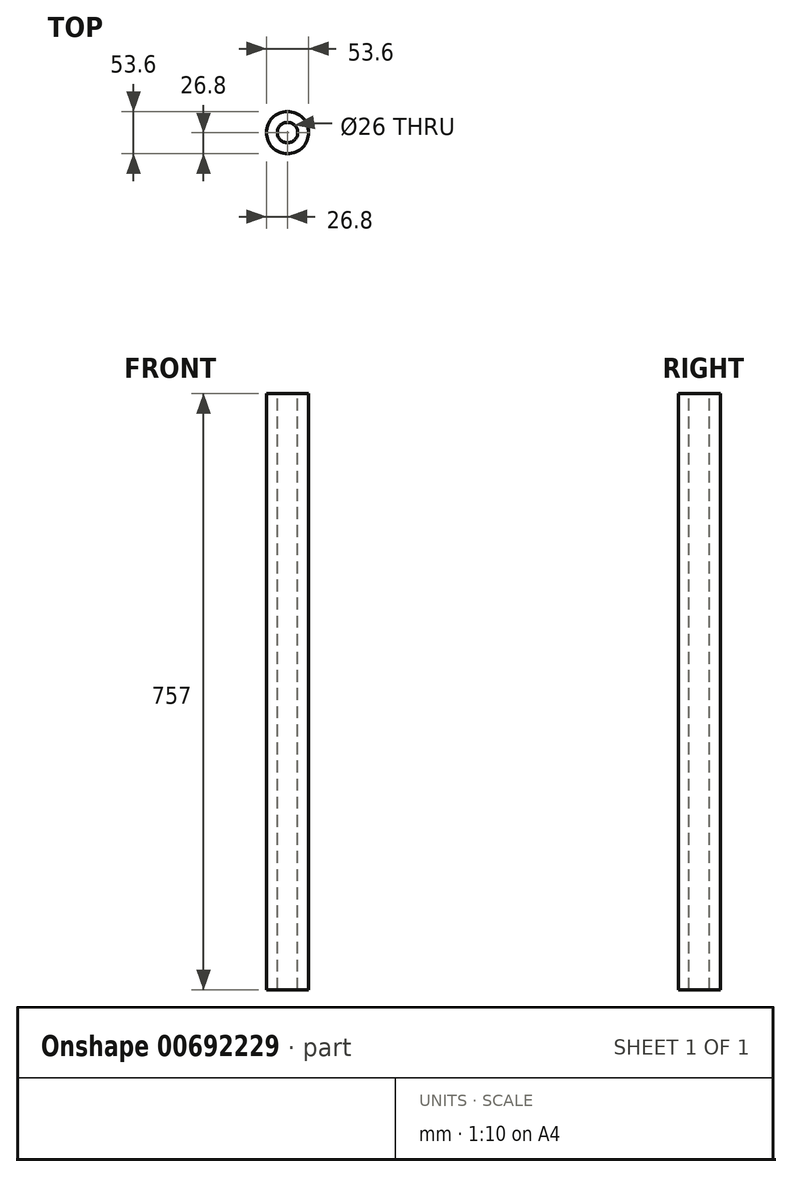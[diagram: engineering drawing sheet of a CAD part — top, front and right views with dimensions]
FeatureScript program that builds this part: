
annotation { "Feature Type Name" : "Feature", "Feature Type Description" : "" }
export const myFeature = defineFeature(function(context is Context, id is Id, definition is map)
    precondition{}
    {
        {
            var Q0;
            Q0=qCreatedBy(makeId("Front.planeOp"),FACE);
            var sketch = newSketch(context, id + "F0", { "sketchPlane" : qUnion([Q0])});
            skLineSegment(sketch, "E0", {"start": v(-26.8, 0) * mm, "end": v(-26.8, 757) * mm});
            skLineSegment(sketch, "E1", {"start": v(-26.8, 757) * mm, "end": v(-13, 757) * mm});
            skLineSegment(sketch, "E2", {"start": v(-13, 757) * mm, "end": v(-13, 0) * mm});
            skLineSegment(sketch, "E3", {"start": v(-13, 0) * mm, "end": v(-26.8, 0) * mm});
            skSolve(sketch);
        }
        {
            var Q0;
            Q0=qCreatedBy(makeId("Front.planeOp"),FACE);
            var sketch = newSketch(context, id + "F1", { "sketchPlane" : qUnion([Q0])});
            skLineSegment(sketch, "E4", {"start": v(0, 0) * mm, "end": v(0, -53.1) * mm});
            skSolve(sketch);
        }
        {
            var Q0;
            Q0 = qSketchRegion(id + "F0", true);
            var Q1;
            Q1=sQuery(id+"F1.wireOp",EDGE,"E4");
            revolve(context, id + "F2", {"entities" : qUnion([Q0]), "axis" : qUnion([Q1]), "revolveType" : RevolveType.FULL});
        }
    });
